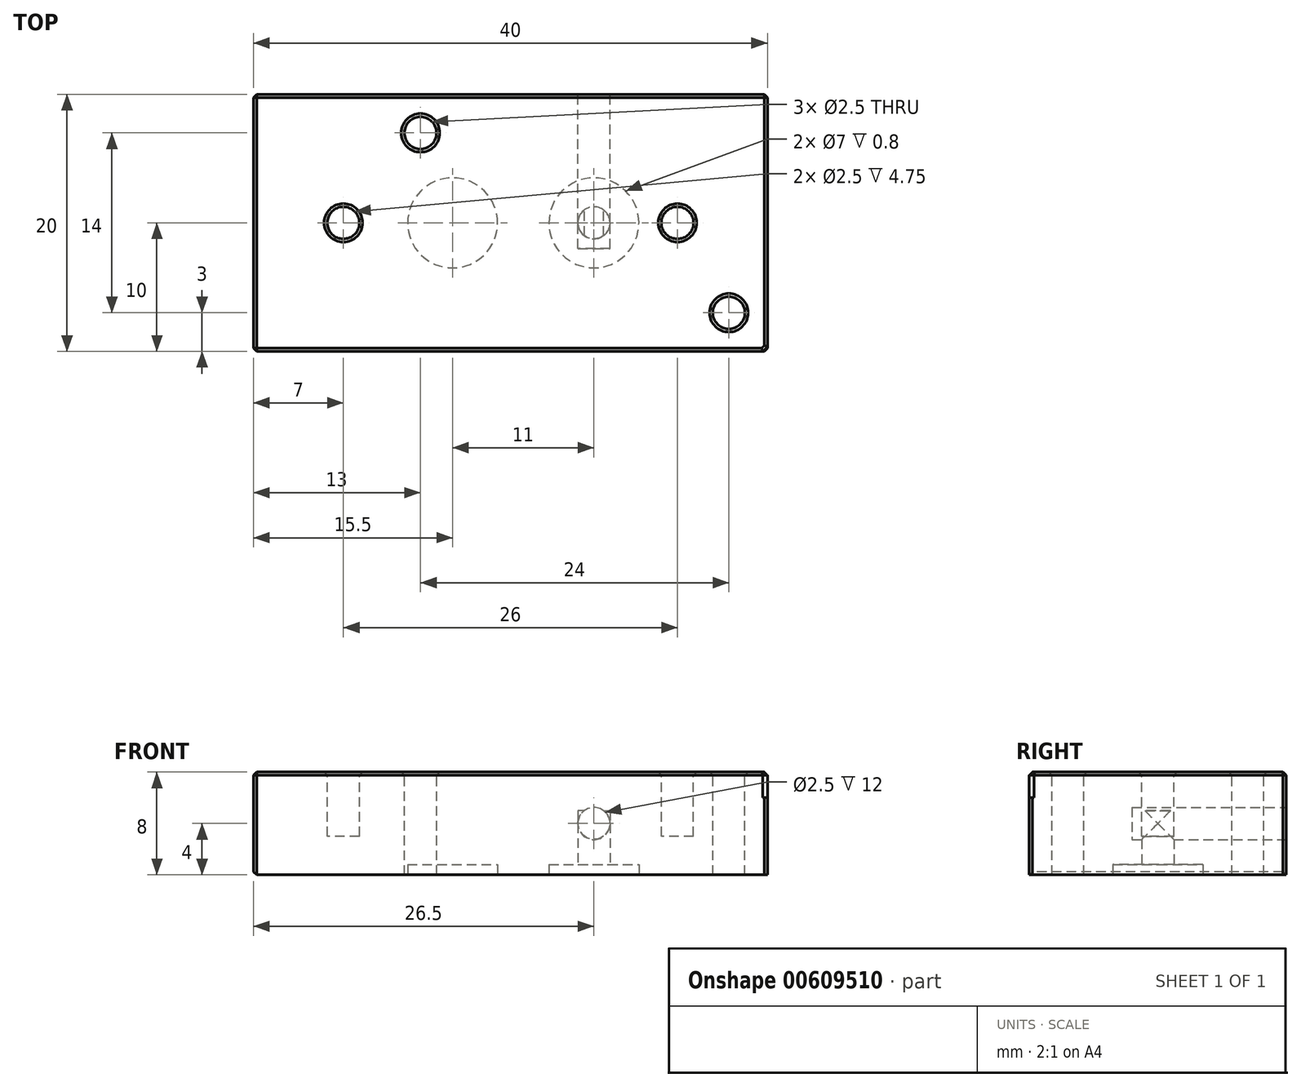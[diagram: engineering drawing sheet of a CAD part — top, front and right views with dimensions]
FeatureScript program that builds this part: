
annotation { "Feature Type Name" : "Feature", "Feature Type Description" : "" }
export const myFeature = defineFeature(function(context is Context, id is Id, definition is map)
    precondition{}
    {
        {
            var Q0;
            Q0=qCreatedBy(makeId("Top.planeOp"),FACE);
            var sketch = newSketch(context, id + "F0", { "sketchPlane" : qUnion([Q0])});
            skLineSegment(sketch, "E0.bottom", {"start": v(0, 0) * mm, "end": v(40, 0) * mm});
            skLineSegment(sketch, "E0.top", {"start": v(0, -20) * mm, "end": v(40, -20) * mm});
            skLineSegment(sketch, "E0.left", {"start": v(0, 0) * mm, "end": v(0, -20) * mm});
            skLineSegment(sketch, "E0.right", {"start": v(40, 0) * mm, "end": v(40, -20) * mm});
            skSolve(sketch);
        }
        {
            var Q0;
            Q0=makeQuery(id+"F0.imprint","IMPRINT",FACE,{"disambiguationData":[TD([[makeQuery(id+"F0.imprint","IMPRINT",EDGE,{"derivedFrom":sQuery(id+"F0.wireOp",EDGE,"E0.bottom")}),-1.0]])]});
            extrude(context, id + "F1", {"entities" : qUnion([Q0]), "depth" : 8 * mm, "offsetDistance" : 25 * mm});
        }
        {
            var Q0;
            Q0=makeQuery(id+"F1.opExtrude","CAP_FACE",FACE,{"disambiguationData":[OSD([sQuery(id+"F0.wireOp",EDGE,"E0.bottom"),sQuery(id+"F0.wireOp",EDGE,"E0.top"),sQuery(id+"F0.wireOp",EDGE,"E0.left"),sQuery(id+"F0.wireOp",EDGE,"E0.right")])],"isStart":false});
            var sketch = newSketch(context, id + "F2", { "sketchPlane" : qUnion([Q0])});
            skLineSegment(sketch, "E1", {"start": v(40, -10) * mm, "end": v(0, -10) * mm, "construction": true});
            skCircle(sketch, "E2", {"center": v(26.5, -10) * mm, "radius": 1.25 * mm});
            skCircle(sketch, "E3", {"center": v(15.5, -10) * mm, "radius": 1.25 * mm});
            skCircle(sketch, "E4", {"center": v(26.5, -10) * mm, "radius": 3 * mm});
            skCircle(sketch, "E5", {"center": v(15.5, -10) * mm, "radius": 3 * mm});
            skLineSegment(sketch, "E6", {"start": v(37, -20) * mm, "end": v(37, -17) * mm, "construction": true});
            skLineSegment(sketch, "E7", {"start": v(37, -17) * mm, "end": v(40, -17) * mm, "construction": true});
            skLineSegment(sketch, "E8", {"start": v(0, -3) * mm, "end": v(13, -3) * mm, "construction": true});
            skLineSegment(sketch, "E9", {"start": v(13, -3) * mm, "end": v(13, 0) * mm, "construction": true});
            skCircle(sketch, "E10", {"center": v(13, -3) * mm, "radius": 1.25 * mm});
            skCircle(sketch, "E11", {"center": v(37, -17) * mm, "radius": 1.25 * mm});
            skArc(sketch, "E12", {"start": v(15.13, -16.25) * mm, "mid": v(13, -14.12) * mm, "end": v(10.88, -16.25) * mm});
            skLineSegment(sketch, "E13", {"start": v(10.88, -16.25) * mm, "end": v(10.88, -20) * mm});
            skLineSegment(sketch, "E14", {"start": v(15.13, -16.25) * mm, "end": v(15.13, -20) * mm});
            skArc(sketch, "E15", {"start": v(34.88, -3.75) * mm, "mid": v(35.5, -5.25) * mm, "end": v(37, -5.88) * mm});
            skLineSegment(sketch, "E16", {"start": v(37, -5.88) * mm, "end": v(40, -5.88) * mm});
            skLineSegment(sketch, "E17", {"start": v(34.88, -3.75) * mm, "end": v(34.88, 0) * mm});
            skSolve(sketch);
        }
        {
            var Q0;
            Q0=makeQuery(id+"F1.opExtrude","CAP_FACE",FACE,{"disambiguationData":[OSD([sQuery(id+"F0.wireOp",EDGE,"E0.bottom"),sQuery(id+"F0.wireOp",EDGE,"E0.top"),sQuery(id+"F0.wireOp",EDGE,"E0.left"),sQuery(id+"F0.wireOp",EDGE,"E0.right")])],"isStart":true});
            var sketch = newSketch(context, id + "F3", { "sketchPlane" : qUnion([Q0])});
            skLineSegment(sketch, "E18.bottom", {"start": v(-8.36, -7.93) * mm, "end": v(37.73, -7.93) * mm});
            skLineSegment(sketch, "E18.top", {"start": v(-8.36, 26.65) * mm, "end": v(37.73, 26.65) * mm});
            skLineSegment(sketch, "E18.left", {"start": v(-8.36, -7.93) * mm, "end": v(-8.36, 26.65) * mm});
            skLineSegment(sketch, "E18.right", {"start": v(37.73, -7.93) * mm, "end": v(37.73, 26.65) * mm});
            skSolve(sketch);
        }
        {
            var Q0;
            Q0=makeQuery(id+"F2.imprint","IMPRINT",FACE,{"disambiguationData":[TD([[makeQuery(id+"F2.imprint","IMPRINT",EDGE,{"derivedFrom":sQuery(id+"F2.wireOp",EDGE,"E10")}),1.0]])]});
            var Q1;
            Q1=makeQuery(id+"F2.imprint","IMPRINT",FACE,{"disambiguationData":[TD([[makeQuery(id+"F2.imprint","IMPRINT",EDGE,{"derivedFrom":sQuery(id+"F2.wireOp",EDGE,"E11")}),1.0]])]});
            extrude(context, id + "F4", {"entities" : qUnion([Q0, Q1]), "operationType" : NewBodyOperationType.REMOVE, "oppositeDirection" : true, "depth" : 25 * mm, "offsetDistance" : 25 * mm});
        }
        {
            var Q0;
            Q0=makeQuery(id+"F1.opExtrude","SWEPT_FACE",FACE,{"disambiguationData":[OSD([sQuery(id+"F0.wireOp",EDGE,"E0.bottom")])]});
            var sketch = newSketch(context, id + "F5", { "sketchPlane" : qUnion([Q0])});
            skLineSegment(sketch, "E19", {"start": v(-40, 4) * mm, "end": v(0, 4) * mm, "construction": true});
            skCircle(sketch, "E20", {"center": v(-26.5, 4) * mm, "radius": 1.25 * mm});
            skSolve(sketch);
        }
        {
            var Q0;
            Q0=makeQuery(id+"F5.imprint","IMPRINT",FACE,{"disambiguationData":[TD([[makeQuery(id+"F5.imprint","IMPRINT",EDGE,{"derivedFrom":sQuery(id+"F5.wireOp",EDGE,"E20")}),1.0]])]});
            extrude(context, id + "F6", {"entities" : qUnion([Q0]), "operationType" : NewBodyOperationType.REMOVE, "oppositeDirection" : true, "depth" : 12 * mm, "offsetDistance" : 25 * mm});
        }
        {
            var Q0;
            Q0=makeQuery(id+"F1.opExtrude","CAP_FACE",FACE,{"disambiguationData":[OSD([sQuery(id+"F0.wireOp",EDGE,"E0.bottom"),sQuery(id+"F0.wireOp",EDGE,"E0.top"),sQuery(id+"F0.wireOp",EDGE,"E0.left"),sQuery(id+"F0.wireOp",EDGE,"E0.right")])],"isStart":true});
            var sketch = newSketch(context, id + "F7", { "sketchPlane" : qUnion([Q0])});
            skLineSegment(sketch, "E21", {"start": v(40, 10) * mm, "end": v(0, 10) * mm, "construction": true});
            skCircle(sketch, "E22", {"center": v(26.5, 10) * mm, "radius": 1.25 * mm});
            skSolve(sketch);
        }
        {
            var Q0;
            Q0=makeQuery(id+"F7.imprint","IMPRINT",FACE,{"disambiguationData":[TD([[makeQuery(id+"F7.imprint","IMPRINT",EDGE,{"derivedFrom":sQuery(id+"F7.wireOp",EDGE,"E22")}),1.0]])]});
            extrude(context, id + "F8", {"entities" : qUnion([Q0]), "operationType" : NewBodyOperationType.REMOVE, "oppositeDirection" : true, "depth" : 5 * mm, "offsetDistance" : 25 * mm});
        }
        {
            var Q0;
            Q0=makeQuery(id+"F1.opExtrude","CAP_FACE",FACE,{"disambiguationData":[OSD([sQuery(id+"F0.wireOp",EDGE,"E0.bottom"),sQuery(id+"F0.wireOp",EDGE,"E0.top"),sQuery(id+"F0.wireOp",EDGE,"E0.left"),sQuery(id+"F0.wireOp",EDGE,"E0.right")])],"isStart":false});
            var sketch = newSketch(context, id + "F9", { "sketchPlane" : qUnion([Q0])});
            skCircle(sketch, "E23", {"center": v(13, -3) * mm, "radius": 4 * mm});
            skCircle(sketch, "E24", {"center": v(37, -17) * mm, "radius": 4 * mm});
            skSolve(sketch);
        }
        {
            var Q0;
            Q0=makeQuery(id+"F9.imprint","IMPRINT",FACE,{"disambiguationData":[TD([[makeQuery(id+"F9.imprint","IMPRINT",EDGE,{"derivedFrom":makeQuery(id+"F4.boolean.opBoolean","COPY",EDGE,{"derivedFrom":makeQuery(id+"F4.opExtrude","CAP_EDGE",EDGE,{"disambiguationData":[OSD([sQuery(id+"F2.wireOp",EDGE,"E11")])],"isStart":true})})}),-1.0]])]});
            var Q1;
            {var subQ0=sQuery(id+"F9.wireOp",EDGE,"E24");var subQ1=makeQuery(id+"F1.opExtrude","CAP_EDGE",EDGE,{"disambiguationData":[OSD([sQuery(id+"F0.wireOp",EDGE,"E0.top")])],"isStart":false});var subQ2=makeQuery(id+"F9.imprint","INTERSECT",VERTEX,{"disambiguationData":[OD(1.0)],"derivedFrom":[subQ1,subQ0]});Q1=makeQuery(id+"F9.imprint","IMPRINT",FACE,{"disambiguationData":[TD([[makeQuery(id+"F9.imprint","IMPRINT",EDGE,{"disambiguationData":[TD([[subQ2,-1.0]])],"derivedFrom":subQ0}),-1.0]])]});}
            var Q2;
            Q2=makeQuery(id+"F9.imprint","IMPRINT",FACE,{"disambiguationData":[TD([[makeQuery(id+"F9.imprint","IMPRINT",EDGE,{"derivedFrom":makeQuery(id+"F4.boolean.opBoolean","COPY",EDGE,{"derivedFrom":makeQuery(id+"F4.opExtrude","CAP_EDGE",EDGE,{"disambiguationData":[OSD([sQuery(id+"F2.wireOp",EDGE,"E10")])],"isStart":true})})}),-1.0]])]});
            extrude(context, id + "F10", {"entities" : qUnion([Q0, Q1, Q2]), "operationType" : NewBodyOperationType.REMOVE, "oppositeDirection" : true, "depth" : 2 * mm, "offsetDistance" : 25 * mm});
        }
        {
            var Q0;
            Q0=makeQuery(id+"F1.opExtrude","CAP_FACE",FACE,{"disambiguationData":[OSD([sQuery(id+"F0.wireOp",EDGE,"E0.bottom"),sQuery(id+"F0.wireOp",EDGE,"E0.top"),sQuery(id+"F0.wireOp",EDGE,"E0.left"),sQuery(id+"F0.wireOp",EDGE,"E0.right")])],"isStart":true});
            var sketch = newSketch(context, id + "F11", { "sketchPlane" : qUnion([Q0])});
            skCircle(sketch, "E25", {"center": v(26.5, 10) * mm, "radius": 2.5 * mm});
            skCircle(sketch, "E26", {"center": v(26.5, 10) * mm, "radius": 3.5 * mm});
            skCircle(sketch, "E27", {"center": v(15.5, 10) * mm, "radius": 2.5 * mm});
            skCircle(sketch, "E28", {"center": v(15.5, 10) * mm, "radius": 3.5 * mm});
            skSolve(sketch);
        }
        {
            var Q0;
            Q0=makeQuery(id+"F11.imprint","IMPRINT",FACE,{"disambiguationData":[TD([[makeQuery(id+"F11.imprint","IMPRINT",EDGE,{"derivedFrom":sQuery(id+"F11.wireOp",EDGE,"E25")}),-1.0]])]});
            var Q1;
            Q1=makeQuery(id+"F11.imprint","IMPRINT",FACE,{"disambiguationData":[TD([[makeQuery(id+"F11.imprint","IMPRINT",EDGE,{"derivedFrom":sQuery(id+"F11.wireOp",EDGE,"E25")}),1.0]])]});
            var Q2;
            Q2=makeQuery(id+"F11.imprint","IMPRINT",FACE,{"disambiguationData":[TD([[makeQuery(id+"F11.imprint","IMPRINT",EDGE,{"derivedFrom":sQuery(id+"F11.wireOp",EDGE,"E27")}),-1.0]])]});
            var Q3;
            Q3=makeQuery(id+"F11.imprint","IMPRINT",FACE,{"disambiguationData":[TD([[makeQuery(id+"F11.imprint","IMPRINT",EDGE,{"derivedFrom":sQuery(id+"F11.wireOp",EDGE,"E27")}),1.0]])]});
            extrude(context, id + "F12", {"entities" : qUnion([Q0, Q1, Q2, Q3]), "operationType" : NewBodyOperationType.REMOVE, "flatOperationType" : FlatOperationType.REMOVE, "oppositeDirection" : true, "depth" : .8 * mm, "offsetDistance" : 25 * mm, "domain" : OperationDomain.MODEL});
        }
        {
            var Q0;
            Q0=makeQuery(id+"F1.opExtrude","CAP_FACE",FACE,{"disambiguationData":[OSD([sQuery(id+"F0.wireOp",EDGE,"E0.bottom"),sQuery(id+"F0.wireOp",EDGE,"E0.top"),sQuery(id+"F0.wireOp",EDGE,"E0.left"),sQuery(id+"F0.wireOp",EDGE,"E0.right")])],"isStart":false});
            var sketch = newSketch(context, id + "F13", { "sketchPlane" : qUnion([Q0])});
            skLineSegment(sketch, "E29", {"start": v(0, -10) * mm, "end": v(40, -10) * mm, "construction": true});
            skCircle(sketch, "E30", {"center": v(7, -10) * mm, "radius": 1.25 * mm});
            skCircle(sketch, "E31", {"center": v(33, -10) * mm, "radius": 1.25 * mm});
            skSolve(sketch);
        }
        {
            var Q0;
            Q0=makeQuery(id+"F13.imprint","IMPRINT",FACE,{"disambiguationData":[TD([[makeQuery(id+"F13.imprint","IMPRINT",EDGE,{"derivedFrom":sQuery(id+"F13.wireOp",EDGE,"E30")}),1.0]])]});
            var Q1;
            Q1=makeQuery(id+"F13.imprint","IMPRINT",FACE,{"disambiguationData":[TD([[makeQuery(id+"F13.imprint","IMPRINT",EDGE,{"derivedFrom":sQuery(id+"F13.wireOp",EDGE,"E31")}),1.0]])]});
            extrude(context, id + "F14", {"entities" : qUnion([Q0, Q1]), "operationType" : NewBodyOperationType.REMOVE, "oppositeDirection" : true, "depth" : 5 * mm, "offsetDistance" : 25 * mm});
        }
        {
            var Q0;
            Q0=makeQuery(id+"F1.opExtrude","CAP_FACE",FACE,{"disambiguationData":[OSD([sQuery(id+"F0.wireOp",EDGE,"E0.bottom"),sQuery(id+"F0.wireOp",EDGE,"E0.top"),sQuery(id+"F0.wireOp",EDGE,"E0.left"),sQuery(id+"F0.wireOp",EDGE,"E0.right")])],"isStart":false});
            var Q1;
            Q1=makeQuery(id+"F6.boolean.opBoolean","COPY",EDGE,{"derivedFrom":makeQuery(id+"F6.opExtrude","CAP_EDGE",EDGE,{"disambiguationData":[OSD([sQuery(id+"F5.wireOp",EDGE,"E20")])],"isStart":true})});
            var Q2;
            Q2=makeQuery(id+"F1.opExtrude","SWEPT_FACE",FACE,{"disambiguationData":[OSD([sQuery(id+"F0.wireOp",EDGE,"E0.left")])]});
            var Q3;
            Q3=makeQuery(id+"F1.opExtrude","SWEPT_EDGE",EDGE,{"disambiguationData":[OSD([sQuery(id+"F0.wireOp",EDGE,"E0.top"),sQuery(id+"F0.wireOp",EDGE,"E0.right")])]});
            var Q4;
            Q4=makeQuery(id+"F1.opExtrude","SWEPT_EDGE",EDGE,{"disambiguationData":[OSD([sQuery(id+"F0.wireOp",EDGE,"E0.bottom"),sQuery(id+"F0.wireOp",EDGE,"E0.right")])]});
            chamfer(context, id + "F15", {"entities" : qUnion([Q0, Q1, Q2, Q3, Q4]), "width" : 0.25 * mm, "tangentPropagation" : true});
        }
    });
